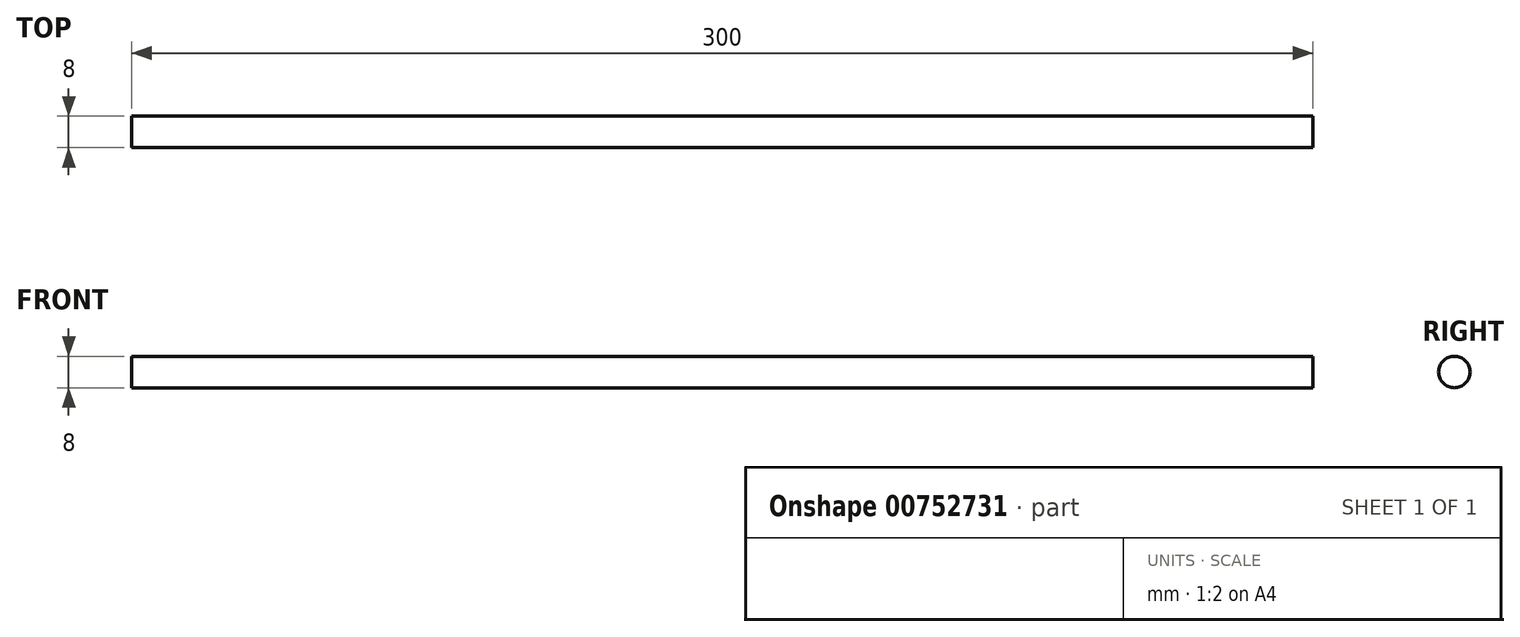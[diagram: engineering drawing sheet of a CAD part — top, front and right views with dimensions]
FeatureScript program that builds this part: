
annotation { "Feature Type Name" : "Feature", "Feature Type Description" : "" }
export const myFeature = defineFeature(function(context is Context, id is Id, definition is map)
    precondition{}
    {
        {
            var Q0;
            Q0=qCreatedBy(makeId("Front.planeOp"),FACE);
            var sketch = newSketch(context, id + "F0", { "sketchPlane" : qUnion([Q0])});
            skLineSegment(sketch, "E0", {"start": v(-150, 0) * mm, "end": v(150, 0) * mm});
            skLineSegment(sketch, "E1.bottom", {"start": v(-150, 4) * mm, "end": v(150, 4) * mm});
            skLineSegment(sketch, "E1.top", {"start": v(-150, -4) * mm, "end": v(150, -4) * mm});
            skLineSegment(sketch, "E1.left", {"start": v(-150, 4) * mm, "end": v(-150, -4) * mm});
            skLineSegment(sketch, "E1.right", {"start": v(150, 4) * mm, "end": v(150, -4) * mm});
            skPoint(sketch, "E1.middle", {"position": v(0, 0) * mm});
            skSolve(sketch);
        }
        {
            var Q0;
            Q0=makeQuery(id+"F0.imprint","IMPRINT",FACE,{"disambiguationData":[TD([[makeQuery(id+"F0.imprint","IMPRINT",EDGE,{"derivedFrom":sQuery(id+"F0.wireOp",EDGE,"E1.bottom")}),-1.0]])]});
            var Q1;
            Q1=sQuery(id+"F0.wireOp",EDGE,"E0");
            revolve(context, id + "F1", {"surfaceOperationType" : NewSurfaceOperationType.NEW, "entities" : qUnion([Q0]), "axis" : qUnion([Q1]), "revolveType" : RevolveType.FULL});
        }
    });
